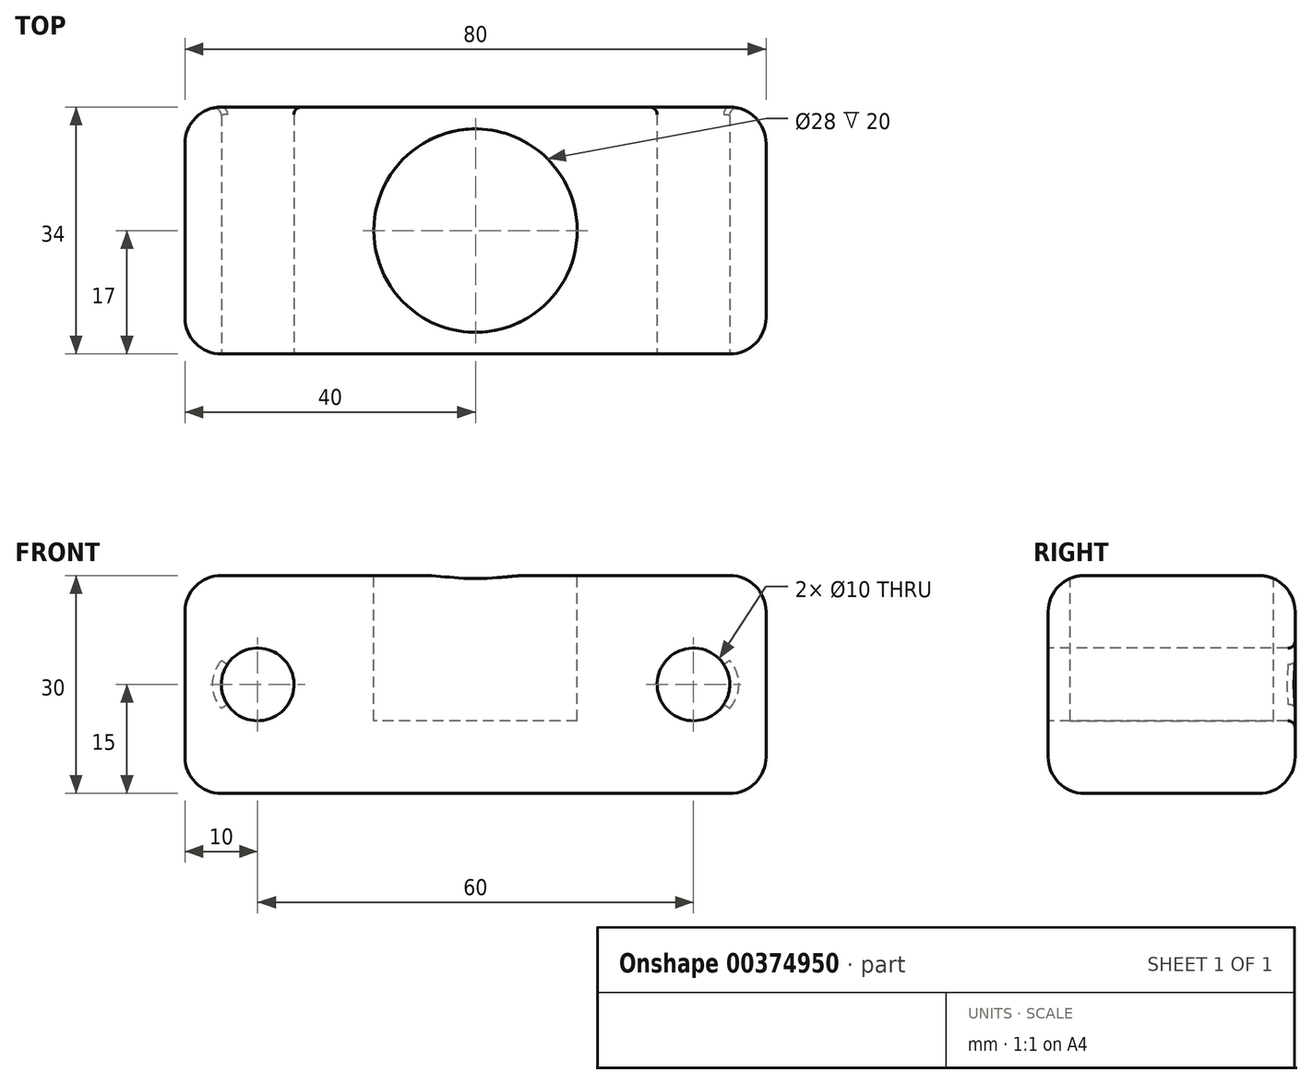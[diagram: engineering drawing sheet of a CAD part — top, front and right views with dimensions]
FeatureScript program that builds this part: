
annotation { "Feature Type Name" : "Feature", "Feature Type Description" : "" }
export const myFeature = defineFeature(function(context is Context, id is Id, definition is map)
    precondition{}
    {
        {
            var Q0;
            Q0=qCreatedBy(makeId("Top.planeOp"),FACE);
            var sketch = newSketch(context, id + "F0", { "sketchPlane" : qUnion([Q0])});
            skLineSegment(sketch, "E0.bottom", {"start": v(40, -17) * mm, "end": v(-40, -17) * mm});
            skLineSegment(sketch, "E0.top", {"start": v(40, 17) * mm, "end": v(-40, 17) * mm});
            skLineSegment(sketch, "E0.left", {"start": v(40, -17) * mm, "end": v(40, 17) * mm});
            skLineSegment(sketch, "E0.right", {"start": v(-40, -17) * mm, "end": v(-40, 17) * mm});
            skPoint(sketch, "E0.middle", {"position": v(0, 0) * mm});
            skSolve(sketch);
        }
        {
            var Q0;
            Q0 = qSketchRegion(id + "F0", true);
            extrude(context, id + "F1", {"entities" : qUnion([Q0]), "oppositeDirection" : true, "depth" : 30 * mm});
        }
        {
            var Q0;
            Q0=makeQuery(id+"F1.opExtrude","SWEPT_FACE",FACE,{"disambiguationData":[OSD([sQuery(id+"F0.wireOp",EDGE,"E0.bottom")])]});
            var sketch = newSketch(context, id + "F2", { "sketchPlane" : qUnion([Q0])});
            skCircle(sketch, "E1", {"center": v(-30, -15) * mm, "radius": 5 * mm});
            skCircle(sketch, "E2", {"center": v(30, -15) * mm, "radius": 5 * mm});
            skSolve(sketch);
        }
        {
            var Q0;
            Q0 = qSketchRegion(id + "F2", true);
            extrude(context, id + "F3", {"entities" : qUnion([Q0]), "operationType" : NewBodyOperationType.REMOVE, "endBound" : BoundingType.THROUGH_ALL, "oppositeDirection" : true, "depth" : 25 * mm});
        }
        {
            var Q0;
            Q0=makeQuery(id+"F1.opExtrude","CAP_FACE",FACE,{"disambiguationData":[OSD([sQuery(id+"F0.wireOp",EDGE,"E0.bottom"),sQuery(id+"F0.wireOp",EDGE,"E0.top"),sQuery(id+"F0.wireOp",EDGE,"E0.left"),sQuery(id+"F0.wireOp",EDGE,"E0.right")])],"isStart":true});
            var sketch = newSketch(context, id + "F4", { "sketchPlane" : qUnion([Q0])});
            skCircle(sketch, "E3", {"center": v(0, 0) * mm, "radius": 14 * mm});
            skCircle(sketch, "E4", {"center": v(0, 0) * mm, "radius": 17 * mm});
            skSolve(sketch);
        }
        {
            var Q0;
            Q0=makeQuery(id+"F4.imprint","IMPRINT",FACE,{"disambiguationData":[TD([[makeQuery(id+"F4.imprint","IMPRINT",EDGE,{"derivedFrom":sQuery(id+"F4.wireOp",EDGE,"E3")}),1.0]])]});
            extrude(context, id + "F5", {"entities" : qUnion([Q0]), "operationType" : NewBodyOperationType.REMOVE, "oppositeDirection" : true, "depth" : 20 * mm});
        }
        {
            var Q0;
            Q0=makeQuery(id+"F1.opExtrude","SWEPT_EDGE",EDGE,{"disambiguationData":[OSD([sQuery(id+"F0.wireOp",EDGE,"E0.bottom"),sQuery(id+"F0.wireOp",EDGE,"E0.left")])]});
            var Q1;
            Q1=makeQuery(id+"F1.opExtrude","SWEPT_EDGE",EDGE,{"disambiguationData":[OSD([sQuery(id+"F0.wireOp",EDGE,"E0.top"),sQuery(id+"F0.wireOp",EDGE,"E0.left")])]});
            var Q2;
            Q2=makeQuery(id+"F1.opExtrude","SWEPT_EDGE",EDGE,{"disambiguationData":[OSD([sQuery(id+"F0.wireOp",EDGE,"E0.bottom"),sQuery(id+"F0.wireOp",EDGE,"E0.right")])]});
            var Q3;
            Q3=makeQuery(id+"F1.opExtrude","SWEPT_EDGE",EDGE,{"disambiguationData":[OSD([sQuery(id+"F0.wireOp",EDGE,"E0.top"),sQuery(id+"F0.wireOp",EDGE,"E0.right")])]});
            var Q4;
            Q4=makeQuery(id+"F1.opExtrude","CAP_EDGE",EDGE,{"disambiguationData":[OSD([sQuery(id+"F0.wireOp",EDGE,"E0.top")])],"isStart":false});
            var Q5;
            Q5=makeQuery(id+"F1.opExtrude","CAP_EDGE",EDGE,{"disambiguationData":[OSD([sQuery(id+"F0.wireOp",EDGE,"E0.right")])],"isStart":false});
            var Q6;
            Q6=makeQuery(id+"F1.opExtrude","CAP_EDGE",EDGE,{"disambiguationData":[OSD([sQuery(id+"F0.wireOp",EDGE,"E0.bottom")])],"isStart":false});
            var Q7;
            Q7=makeQuery(id+"F1.opExtrude","CAP_EDGE",EDGE,{"disambiguationData":[OSD([sQuery(id+"F0.wireOp",EDGE,"E0.left")])],"isStart":false});
            var Q8;
            Q8=makeQuery(id+"F1.opExtrude","CAP_EDGE",EDGE,{"disambiguationData":[OSD([sQuery(id+"F0.wireOp",EDGE,"E0.bottom")])],"isStart":true});
            var Q9;
            Q9=makeQuery(id+"F1.opExtrude","CAP_EDGE",EDGE,{"disambiguationData":[OSD([sQuery(id+"F0.wireOp",EDGE,"E0.top")])],"isStart":true});
            fillet(context, id + "F6", {"entities" : qUnion([Q0, Q1, Q2, Q3, Q4, Q5, Q6, Q7, Q8, Q9]), "radius" : 5 * mm, "tangentPropagation" : true, "allowEdgeOverflow" : false});
        }
        {
            var Q0;
            Q0=makeQuery(id+"FtnS2kDMG1GThNu_1.boolean.opBoolean","COPY",EDGE,{"derivedFrom":makeQuery(id+"FtnS2kDMG1GThNu_1.opExtrude","CAP_EDGE",EDGE,{"disambiguationData":[OSD([sQuery(id+"Fik8Zv1LFshMYbS_1.wireOp",EDGE,"pbXum5Yb-NBy9-zFGR-Ce42-xLzdNY24IffF.top")])],"isStart":false})});
            var Q1;
            Q1=makeQuery(id+"FtnS2kDMG1GThNu_1.boolean.opBoolean","COPY",EDGE,{"derivedFrom":makeQuery(id+"FtnS2kDMG1GThNu_1.opExtrude","CAP_EDGE",EDGE,{"disambiguationData":[OSD([sQuery(id+"Fik8Zv1LFshMYbS_1.wireOp",EDGE,"pbXum5Yb-NBy9-zFGR-Ce42-xLzdNY24IffF.bottom")])],"isStart":false})});
            var Q2;
            {var subQ0=sQuery(id+"F0.wireOp",EDGE,"E0.top");Q2=makeQuery(id+"FvvA8nlu8grQD2Z_1.opFillet","BLEND_EDGE",EDGE,{"blendedFrom":[makeQuery(id+"FtnS2kDMG1GThNu_1.boolean.opBoolean","COPY",EDGE,{"derivedFrom":makeQuery(id+"FtnS2kDMG1GThNu_1.opExtrude","SWEPT_EDGE",EDGE,{"disambiguationData":[OSD([subQ0,sQuery(id+"Fik8Zv1LFshMYbS_1.wireOp",EDGE,"VPv0Nvlg-h3A1-stcG-xMFi-ggb0sWrEq8Nb.top"),sQuery(id+"Fik8Zv1LFshMYbS_1.wireOp",EDGE,"VPv0Nvlg-h3A1-stcG-xMFi-ggb0sWrEq8Nb.right")])]})}),makeQuery(id+"F1.opExtrude","CAP_FACE",FACE,{"disambiguationData":[OSD([sQuery(id+"F0.wireOp",EDGE,"E0.bottom"),subQ0,sQuery(id+"F0.wireOp",EDGE,"E0.left"),sQuery(id+"F0.wireOp",EDGE,"E0.right")])],"isStart":true})],"blendedInto":[makeQuery(id+"F1.opExtrude","CAP_FACE",FACE,{"disambiguationData":[OSD([sQuery(id+"F0.wireOp",EDGE,"E0.bottom"),subQ0,sQuery(id+"F0.wireOp",EDGE,"E0.left"),sQuery(id+"F0.wireOp",EDGE,"E0.right")])],"isStart":true})]});}
            var Q3;
            Q3=makeQuery(id+"F5.boolean.opBoolean","COPY",EDGE,{"derivedFrom":makeQuery(id+"F5.opExtrude","CAP_EDGE",EDGE,{"disambiguationData":[OSD([sQuery(id+"F4.wireOp",EDGE,"E3")])],"isStart":true})});
            var Q4;
            Q4=makeQuery(id+"F3.boolean.opBoolean","INTERSECT",EDGE,{"derivedFrom":[makeQuery(id+"F1.opExtrude","SWEPT_FACE",FACE,{"disambiguationData":[OSD([sQuery(id+"F0.wireOp",EDGE,"E0.top")])]}),makeQuery(id+"F3.opExtrude","SWEPT_FACE",FACE,{"disambiguationData":[OSD([sQuery(id+"F2.wireOp",EDGE,"E1")])]})]});
            var Q5;
            Q5=makeQuery(id+"F3.boolean.opBoolean","INTERSECT",EDGE,{"derivedFrom":[makeQuery(id+"F1.opExtrude","SWEPT_FACE",FACE,{"disambiguationData":[OSD([sQuery(id+"F0.wireOp",EDGE,"E0.top")])]}),makeQuery(id+"F3.opExtrude","SWEPT_FACE",FACE,{"disambiguationData":[OSD([sQuery(id+"F2.wireOp",EDGE,"E2")])]})]});
            var Q6;
            Q6=makeQuery(id+"F3.boolean.opBoolean","COPY",EDGE,{"derivedFrom":makeQuery(id+"F3.opExtrude","CAP_EDGE",EDGE,{"disambiguationData":[OSD([sQuery(id+"F2.wireOp",EDGE,"E1")])],"isStart":true})});
            var Q7;
            Q7=makeQuery(id+"F3.boolean.opBoolean","COPY",EDGE,{"derivedFrom":makeQuery(id+"F3.opExtrude","CAP_EDGE",EDGE,{"disambiguationData":[OSD([sQuery(id+"F2.wireOp",EDGE,"E2")])],"isStart":true})});
            fillet(context, id + "F7", {"entities" : qUnion([Q0, Q1, Q2, Q3, Q4, Q5, Q6, Q7]), "radius" : 1 * mm, "tangentPropagation" : true, "allowEdgeOverflow" : false});
        }
        {
            var Q0;
            Q0=makeQuery(id+"F1.opExtrude","CAP_EDGE",EDGE,{"disambiguationData":[OSD([sQuery(id+"F0.wireOp",EDGE,"E0.right")])],"isStart":true});
            var Q1;
            Q1=makeQuery(id+"F1.opExtrude","CAP_EDGE",EDGE,{"disambiguationData":[OSD([sQuery(id+"F0.wireOp",EDGE,"E0.left")])],"isStart":true});
            fillet(context, id + "F8", {"entities" : qUnion([Q0, Q1]), "radius" : 5 * mm, "tangentPropagation" : true, "allowEdgeOverflow" : false});
        }
    });
